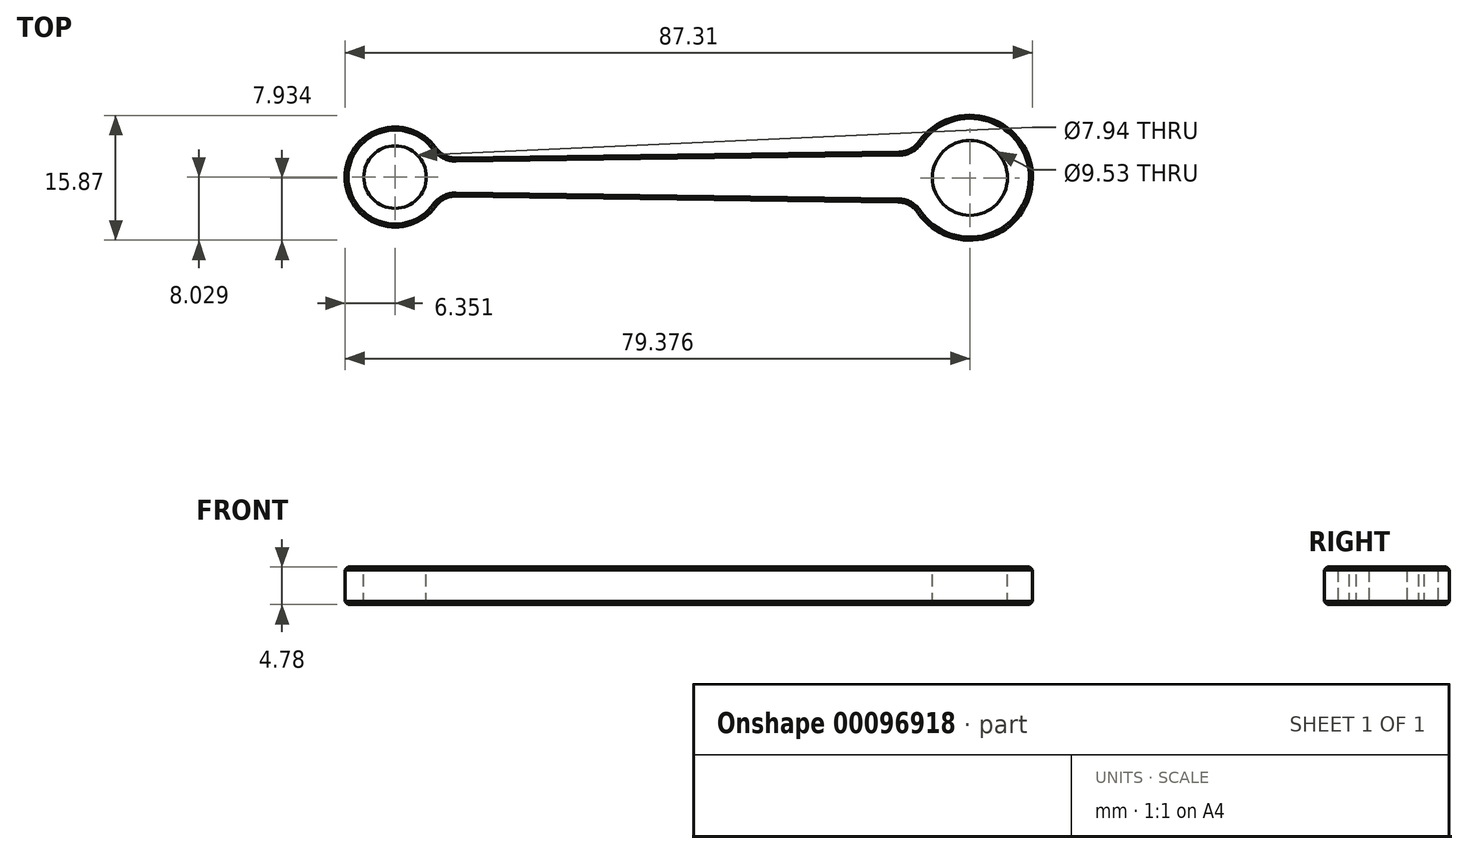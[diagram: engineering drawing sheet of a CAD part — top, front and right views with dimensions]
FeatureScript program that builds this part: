
annotation { "Feature Type Name" : "Feature", "Feature Type Description" : "" }
export const myFeature = defineFeature(function(context is Context, id is Id, definition is map)
    precondition{}
    {
        {
            var Q0;
            Q0=qCreatedBy(makeId("Top.planeOp"),FACE);
            var sketch = newSketch(context, id + "F0", { "sketchPlane" : qUnion([Q0])});
            skArc(sketch, "E0", {"start": v(22.8, -2.99) * mm, "mid": v(37.31, 1.38) * mm, "end": v(22.9, 6.05) * mm});
            skArc(sketch, "E1", {"start": v(-38.5, 5.28) * mm, "mid": v(-50, 1.56) * mm, "end": v(-38.5, -2.17) * mm});
            skLineSegment(sketch, "E2", {"start": v(-54.5, 1.56) * mm, "end": v(44.63, 1.56) * mm, "construction": true});
            skLineSegment(sketch, "E3", {"start": v(29.38, 13.88) * mm, "end": v(29.38, -13.99) * mm, "construction": true});
            skLineSegment(sketch, "E4", {"start": v(-43.65, 11.04) * mm, "end": v(-43.65, -10.39) * mm, "construction": true});
            skLineSegment(sketch, "E5", {"start": v(-37.3, -0.83) * mm, "end": v(-50.77, -0.83) * mm, "construction": true});
            skLineSegment(sketch, "E6", {"start": v(21.44, -1.62) * mm, "end": v(28.22, -1.62) * mm, "construction": true});
            skLineSegment(sketch, "E7", {"start": v(20.35, 4.71) * mm, "end": v(-35.9, 3.97) * mm});
            skLineSegment(sketch, "E8", {"start": v(-35.9, -0.85) * mm, "end": v(20.22, -1.6) * mm});
            skPoint(sketch, "E9.visualSharp", {"position": v(-37.77, 3.95) * mm});
            skArc(sketch, "E9.filletArc", {"start": v(-38.5, 5.28) * mm, "mid": v(-37.36, 4.3) * mm, "end": v(-35.9, 3.97) * mm});
            skPoint(sketch, "E10.visualSharp", {"position": v(-37.77, -0.83) * mm});
            skArc(sketch, "E10.filletArc", {"start": v(-35.9, -0.85) * mm, "mid": v(-37.36, -1.2) * mm, "end": v(-38.5, -2.17) * mm});
            skPoint(sketch, "E11.visualSharp", {"position": v(22.06, -1.62) * mm});
            skArc(sketch, "E11.filletArc", {"start": v(22.8, -2.99) * mm, "mid": v(21.68, -1.97) * mm, "end": v(20.22, -1.6) * mm});
            skArc(sketch, "E12.filletArc", {"start": v(20.35, 4.71) * mm, "mid": v(21.78, 5.07) * mm, "end": v(22.9, 6.05) * mm});
            skSolve(sketch);
        }
        {
            var Q0;
            Q0=makeQuery(id+"F0.imprint","IMPRINT",FACE,{"disambiguationData":[TD([[makeQuery(id+"F0.imprint","IMPRINT",EDGE,{"derivedFrom":sQuery(id+"F0.wireOp",EDGE,"E0")}),1.0]])]});
            extrude(context, id + "F1", {"entities" : qUnion([Q0]), "depth" : 4.78 * mm});
        }
        {
            var Q0;
            Q0=makeQuery(id+"F1.opExtrude","CAP_FACE",FACE,{"disambiguationData":[OSD([sQuery(id+"F0.wireOp",EDGE,"E0"),sQuery(id+"F0.wireOp",EDGE,"E1"),sQuery(id+"F0.wireOp",EDGE,"E7"),sQuery(id+"F0.wireOp",EDGE,"E8"),sQuery(id+"F0.wireOp",EDGE,"E9.filletArc"),sQuery(id+"F0.wireOp",EDGE,"E10.filletArc"),sQuery(id+"F0.wireOp",EDGE,"E11.filletArc"),sQuery(id+"F0.wireOp",EDGE,"E12.filletArc")])],"isStart":false});
            var sketch = newSketch(context, id + "F2", { "sketchPlane" : qUnion([Q0])});
            skLineSegment(sketch, "E13", {"start": v(-43.65, 1.56) * mm, "end": v(-43.65, 12.37) * mm, "construction": true});
            skCircle(sketch, "E14", {"center": v(-43.65, 1.56) * mm, "radius": 3.97 * mm});
            skSolve(sketch);
        }
        {
            var Q0;
            Q0=makeQuery(id+"F2.imprint","IMPRINT",FACE,{"disambiguationData":[TD([[makeQuery(id+"F2.imprint","IMPRINT",EDGE,{"derivedFrom":sQuery(id+"F2.wireOp",EDGE,"E14")}),1.0]])]});
            extrude(context, id + "F3", {"entities" : qUnion([Q0]), "operationType" : NewBodyOperationType.REMOVE, "endBound" : BoundingType.THROUGH_ALL, "oppositeDirection" : true, "depth" : 25.4 * mm});
        }
        {
            var Q0;
            Q0=makeQuery(id+"F1.opExtrude","CAP_FACE",FACE,{"disambiguationData":[OSD([sQuery(id+"F0.wireOp",EDGE,"E0"),sQuery(id+"F0.wireOp",EDGE,"E1"),sQuery(id+"F0.wireOp",EDGE,"E7"),sQuery(id+"F0.wireOp",EDGE,"E8"),sQuery(id+"F0.wireOp",EDGE,"E9.filletArc"),sQuery(id+"F0.wireOp",EDGE,"E10.filletArc"),sQuery(id+"F0.wireOp",EDGE,"E11.filletArc"),sQuery(id+"F0.wireOp",EDGE,"E12.filletArc")])],"isStart":false});
            var sketch = newSketch(context, id + "F4", { "sketchPlane" : qUnion([Q0])});
            skLineSegment(sketch, "E15", {"start": v(29.38, 1.46) * mm, "end": v(29.38, 12.67) * mm, "construction": true});
            skCircle(sketch, "E16", {"center": v(29.38, 1.46) * mm, "radius": 4.76 * mm});
            skSolve(sketch);
        }
        {
            var Q0;
            Q0=makeQuery(id+"F4.imprint","IMPRINT",FACE,{"disambiguationData":[TD([[makeQuery(id+"F4.imprint","IMPRINT",EDGE,{"derivedFrom":sQuery(id+"F4.wireOp",EDGE,"E16")}),1.0]])]});
            extrude(context, id + "F5", {"entities" : qUnion([Q0]), "operationType" : NewBodyOperationType.REMOVE, "endBound" : BoundingType.THROUGH_ALL, "oppositeDirection" : true, "depth" : 25.4 * mm});
        }
        {
            var Q0;
            Q0=makeQuery(id+"F1.opExtrude","CAP_EDGE",EDGE,{"disambiguationData":[OSD([sQuery(id+"F0.wireOp",EDGE,"E0")])],"isStart":false});
            var Q1;
            Q1=makeQuery(id+"F1.opExtrude","CAP_EDGE",EDGE,{"disambiguationData":[OSD([sQuery(id+"F0.wireOp",EDGE,"E12.filletArc")])],"isStart":false});
            var Q2;
            Q2=makeQuery(id+"F1.opExtrude","CAP_EDGE",EDGE,{"disambiguationData":[OSD([sQuery(id+"F0.wireOp",EDGE,"E7")])],"isStart":false});
            var Q3;
            Q3=makeQuery(id+"F1.opExtrude","CAP_EDGE",EDGE,{"disambiguationData":[OSD([sQuery(id+"F0.wireOp",EDGE,"E11.filletArc")])],"isStart":false});
            var Q4;
            Q4=makeQuery(id+"F1.opExtrude","CAP_EDGE",EDGE,{"disambiguationData":[OSD([sQuery(id+"F0.wireOp",EDGE,"E8")])],"isStart":false});
            var Q5;
            Q5=makeQuery(id+"F1.opExtrude","CAP_EDGE",EDGE,{"disambiguationData":[OSD([sQuery(id+"F0.wireOp",EDGE,"E9.filletArc")])],"isStart":false});
            var Q6;
            Q6=makeQuery(id+"F1.opExtrude","CAP_EDGE",EDGE,{"disambiguationData":[OSD([sQuery(id+"F0.wireOp",EDGE,"E1")])],"isStart":false});
            var Q7;
            Q7=makeQuery(id+"F1.opExtrude","CAP_EDGE",EDGE,{"disambiguationData":[OSD([sQuery(id+"F0.wireOp",EDGE,"E10.filletArc")])],"isStart":false});
            chamfer(context, id + "F6", {"entities" : qUnion([Q0, Q1, Q2, Q3, Q4, Q5, Q6, Q7]), "width" : 0.38 * mm, "tangentPropagation" : true});
        }
        {
            var Q0;
            Q0=makeQuery(id+"F1.opExtrude","CAP_EDGE",EDGE,{"disambiguationData":[OSD([sQuery(id+"F0.wireOp",EDGE,"E1")])],"isStart":true});
            var Q1;
            Q1=makeQuery(id+"F1.opExtrude","CAP_EDGE",EDGE,{"disambiguationData":[OSD([sQuery(id+"F0.wireOp",EDGE,"E10.filletArc")])],"isStart":true});
            var Q2;
            Q2=makeQuery(id+"F1.opExtrude","CAP_EDGE",EDGE,{"disambiguationData":[OSD([sQuery(id+"F0.wireOp",EDGE,"E9.filletArc")])],"isStart":true});
            var Q3;
            Q3=makeQuery(id+"F1.opExtrude","CAP_EDGE",EDGE,{"disambiguationData":[OSD([sQuery(id+"F0.wireOp",EDGE,"E8")])],"isStart":true});
            var Q4;
            Q4=makeQuery(id+"F1.opExtrude","CAP_EDGE",EDGE,{"disambiguationData":[OSD([sQuery(id+"F0.wireOp",EDGE,"E7")])],"isStart":true});
            var Q5;
            Q5=makeQuery(id+"F1.opExtrude","CAP_EDGE",EDGE,{"disambiguationData":[OSD([sQuery(id+"F0.wireOp",EDGE,"E11.filletArc")])],"isStart":true});
            var Q6;
            Q6=makeQuery(id+"F1.opExtrude","CAP_EDGE",EDGE,{"disambiguationData":[OSD([sQuery(id+"F0.wireOp",EDGE,"E0")])],"isStart":true});
            var Q7;
            Q7=makeQuery(id+"F1.opExtrude","CAP_EDGE",EDGE,{"disambiguationData":[OSD([sQuery(id+"F0.wireOp",EDGE,"E12.filletArc")])],"isStart":true});
            chamfer(context, id + "F7", {"entities" : qUnion([Q0, Q1, Q2, Q3, Q4, Q5, Q6, Q7]), "width" : 0.38 * mm, "tangentPropagation" : true});
        }
    });
